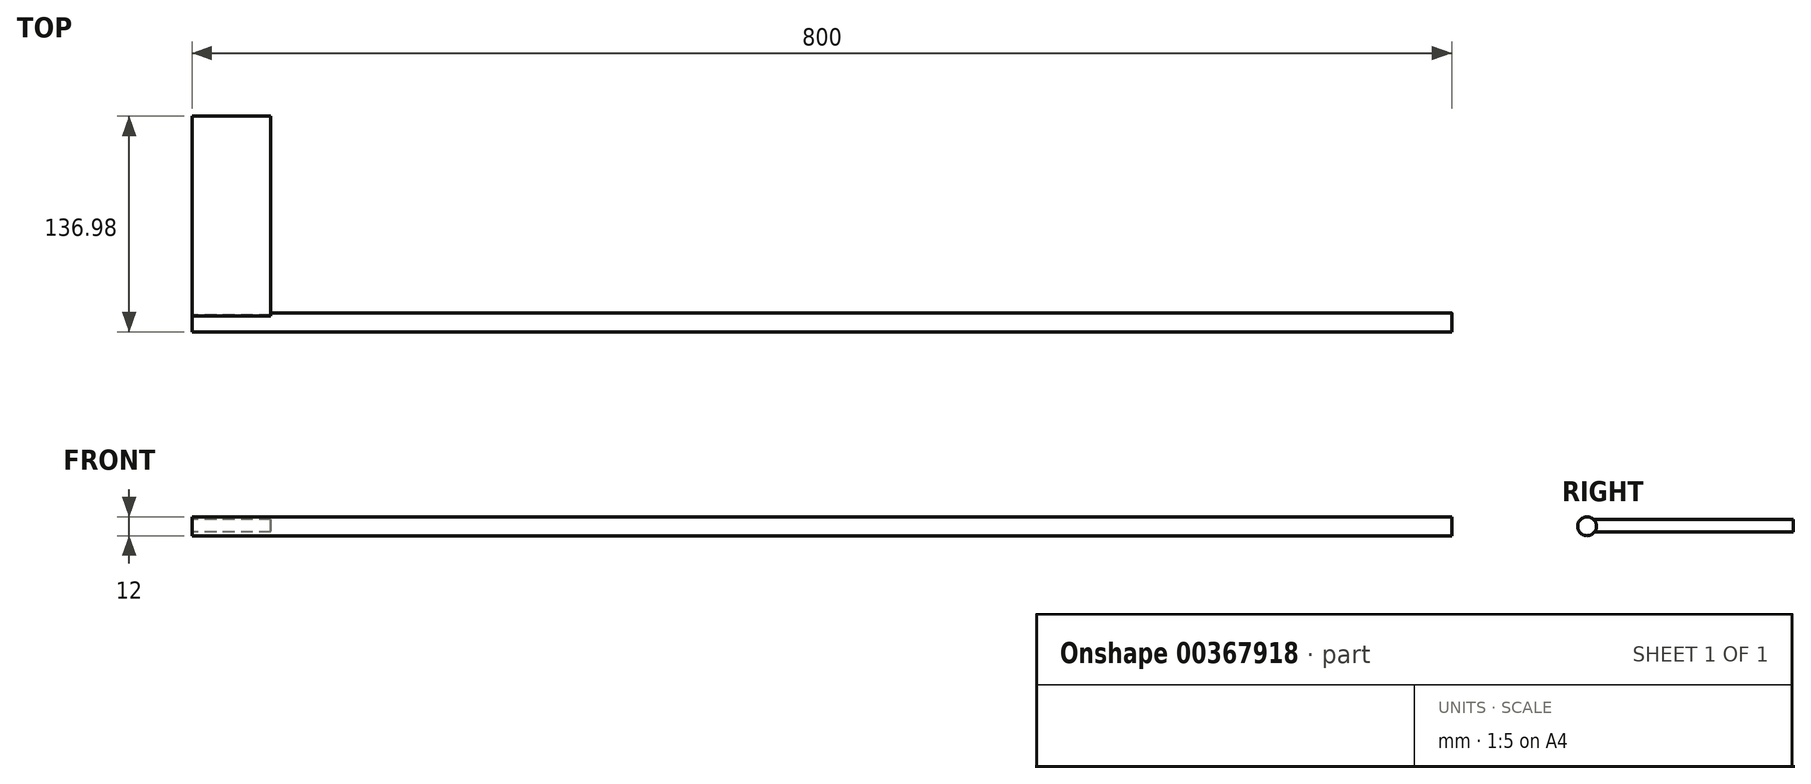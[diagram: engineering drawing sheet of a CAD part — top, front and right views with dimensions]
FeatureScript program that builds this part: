
annotation { "Feature Type Name" : "Feature", "Feature Type Description" : "" }
export const myFeature = defineFeature(function(context is Context, id is Id, definition is map)
    precondition{}
    {
        {
            var Q0;
            Q0=qCreatedBy(makeId("Right.planeOp"),FACE);
            var sketch = newSketch(context, id + "F0", { "sketchPlane" : qUnion([Q0])});
            skCircle(sketch, "E0", {"center": v(-3.98, -6.15) * mm, "radius": 6 * mm});
            skLineSegment(sketch, "E1.bottom", {"start": v(0, -1.67) * mm, "end": v(127, -1.67) * mm});
            skLineSegment(sketch, "E1.top", {"start": v(0, -9.77) * mm, "end": v(127, -9.77) * mm});
            skLineSegment(sketch, "E1.left", {"start": v(0, -1.67) * mm, "end": v(0, -9.77) * mm});
            skLineSegment(sketch, "E1.right", {"start": v(127, -1.67) * mm, "end": v(127, -9.77) * mm});
            skSolve(sketch);
        }
        {
            var Q0;
            {var subQ0=sQuery(id+"F0.wireOp",EDGE,"E1.left");Q0=makeQuery(id+"F0.imprint","IMPRINT",FACE,{"disambiguationData":[TD([[makeQuery(id+"F0.imprint","IMPRINT",EDGE,{"derivedFrom":subQ0}),-1.0]])]});}
            var Q1;
            {var subQ0=sQuery(id+"F0.wireOp",EDGE,"E1.left");Q1=makeQuery(id+"F0.imprint","IMPRINT",FACE,{"disambiguationData":[TD([[makeQuery(id+"F0.imprint","IMPRINT",EDGE,{"derivedFrom":subQ0}),1.0]])]});}
            extrude(context, id + "F1", {"entities" : qUnion([Q0, Q1]), "depth" : 800 * mm});
        }
        {
            var Q0;
            {var subQ0=sQuery(id+"F0.wireOp",EDGE,"E1.bottom");Q0=makeQuery(id+"F0.imprint","IMPRINT",FACE,{"disambiguationData":[TD([[makeQuery(id+"F0.imprint","IMPRINT",EDGE,{"derivedFrom":subQ0}),-1.0]])]});}
            extrude(context, id + "F2", {"entities" : qUnion([Q0]), "operationType" : NewBodyOperationType.ADD, "depth" : 50 * mm});
        }
    });
